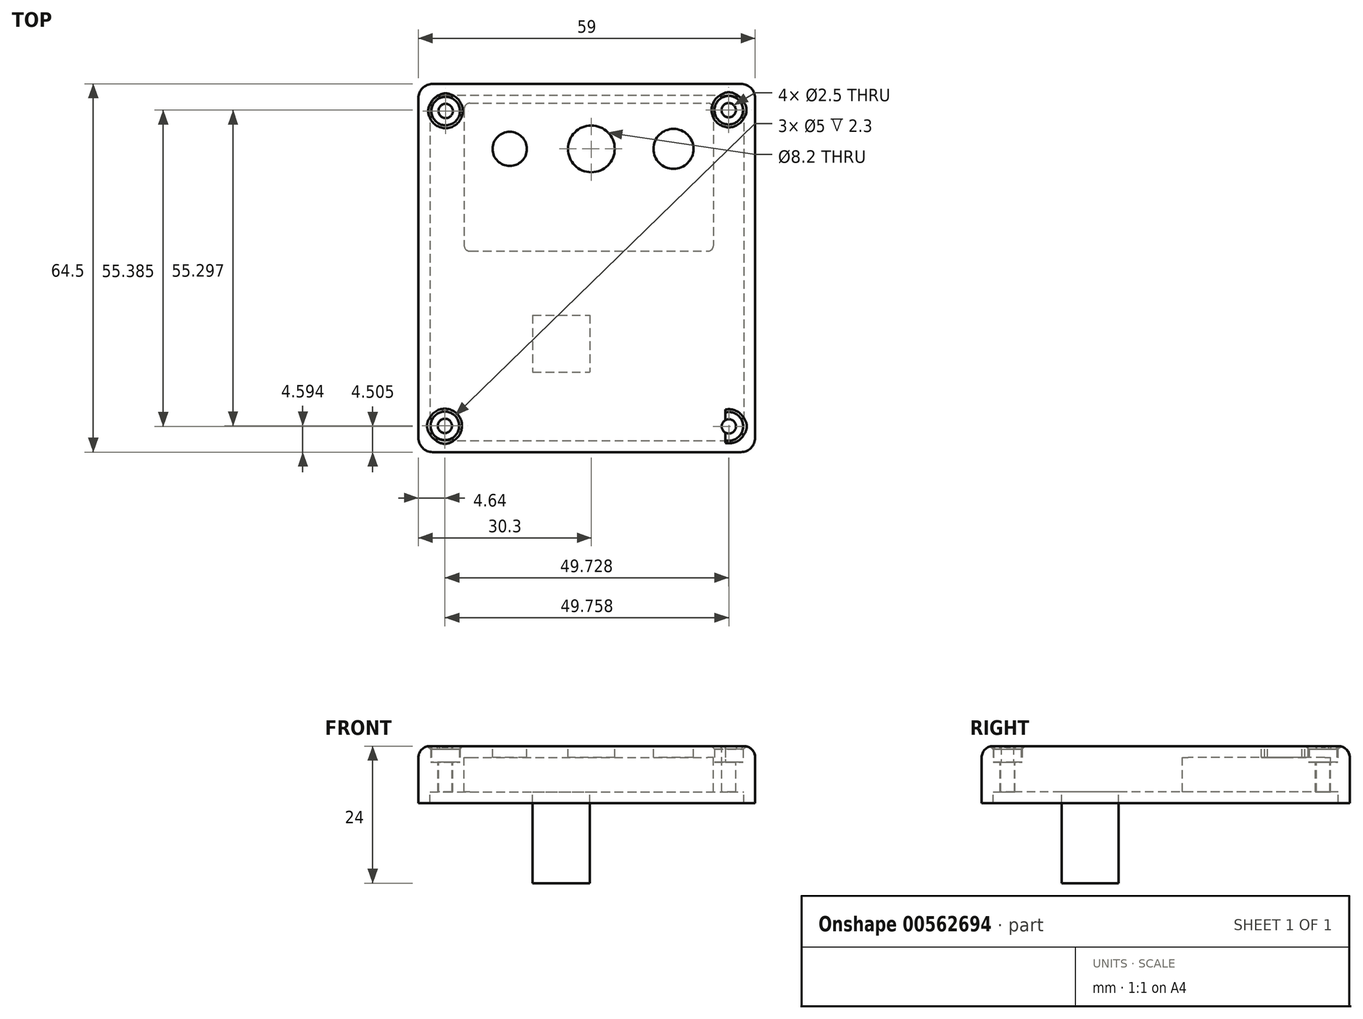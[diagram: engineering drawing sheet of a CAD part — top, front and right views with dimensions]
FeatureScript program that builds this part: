
annotation { "Feature Type Name" : "Feature", "Feature Type Description" : "" }
export const myFeature = defineFeature(function(context is Context, id is Id, definition is map)
    precondition{}
    {
        {
            var Q0;
            Q0=qCreatedBy(makeId("Top.planeOp"),FACE);
            var sketch = newSketch(context, id + "F0", { "sketchPlane" : qUnion([Q0])});
            skLineSegment(sketch, "E0.bottom", {"start": v(-36.58, 47.75) * mm, "end": v(22.42, 47.75) * mm});
            skLineSegment(sketch, "E0.top", {"start": v(-36.58, -16.75) * mm, "end": v(22.42, -16.75) * mm});
            skLineSegment(sketch, "E0.left", {"start": v(-36.58, 47.75) * mm, "end": v(-36.58, -16.75) * mm});
            skLineSegment(sketch, "E0.right", {"start": v(22.42, 47.75) * mm, "end": v(22.42, -16.75) * mm});
            skLineSegment(sketch, "E1.bottom", {"start": v(-34.58, 45.75) * mm, "end": v(20.42, 45.75) * mm});
            skLineSegment(sketch, "E1.top", {"start": v(-34.58, -14.75) * mm, "end": v(20.42, -14.75) * mm});
            skLineSegment(sketch, "E1.left", {"start": v(-34.58, 45.75) * mm, "end": v(-34.58, -14.75) * mm});
            skLineSegment(sketch, "E1.right", {"start": v(20.42, 45.75) * mm, "end": v(20.42, -14.75) * mm});
            skLineSegment(sketch, "E2.right", {"start": v(-34.58, -2) * mm, "end": v(-34.58, 2) * mm});
            skLineSegment(sketch, "E3.bottom", {"start": v(-34.58, 45.75) * mm, "end": v(9.72, 45.75) * mm});
            skLineSegment(sketch, "E4.top", {"start": v(-34.58, -14.75) * mm, "end": v(-32.58, -14.75) * mm});
            skLineSegment(sketch, "E4.left", {"start": v(-34.58, -8.75) * mm, "end": v(-34.58, -14.75) * mm});
            skLineSegment(sketch, "E5.bottom", {"start": v(13.36, 45.75) * mm, "end": v(14.86, 45.75) * mm});
            skLineSegment(sketch, "E6.top", {"start": v(16.3, -14.75) * mm, "end": v(14.92, -14.75) * mm});
            skLineSegment(sketch, "E7.bottom", {"start": v(17.21, 9.77) * mm, "end": v(11.21, 9.77) * mm});
            skLineSegment(sketch, "E7.top", {"start": v(17.21, 4.77) * mm, "end": v(11.21, 4.77) * mm});
            skLineSegment(sketch, "E7.left", {"start": v(17.21, 9.77) * mm, "end": v(17.21, 4.77) * mm});
            skLineSegment(sketch, "E7.right", {"start": v(11.21, 9.77) * mm, "end": v(11.21, 4.77) * mm});
            skCircle(sketch, "E8", {"center": v(-31.94, -12.16) * mm, "radius": 1.25 * mm});
            skCircle(sketch, "E9", {"center": v(-31.8, 43) * mm, "radius": 2.5 * mm});
            skCircle(sketch, "E10", {"center": v(-31.8, 43) * mm, "radius": 1.25 * mm});
            skLineSegment(sketch, "E11", {"start": v(-29.3, 43) * mm, "end": v(-29.3, 45.75) * mm});
            skLineSegment(sketch, "E12.bottom", {"start": v(17.22, 16.75) * mm, "end": v(-34.58, 16.75) * mm});
            skLineSegment(sketch, "E12.top", {"start": v(17.22, 15.25) * mm, "end": v(-34.58, 15.25) * mm});
            skLineSegment(sketch, "E12.left", {"start": v(17.22, 15.25) * mm, "end": v(17.22, 16.75) * mm});
            skLineSegment(sketch, "E12.right", {"start": v(-34.58, 15.25) * mm, "end": v(-34.58, 16.75) * mm});
            skLineSegment(sketch, "E13.bottom", {"start": v(-34.58, 14.63) * mm, "end": v(-32.58, 14.63) * mm});
            skLineSegment(sketch, "E13.top", {"start": v(-34.58, 8.63) * mm, "end": v(-32.58, 8.63) * mm});
            skLineSegment(sketch, "E13.left", {"start": v(-34.58, 14.63) * mm, "end": v(-34.58, 8.63) * mm});
            skLineSegment(sketch, "E13.right", {"start": v(-32.58, 14.63) * mm, "end": v(-32.58, 8.63) * mm});
            skCircle(sketch, "E14", {"center": v(17.79, 43.14) * mm, "radius": 2.5 * mm});
            skCircle(sketch, "E15", {"center": v(17.79, 43.14) * mm, "radius": 1.25 * mm});
            skLineSegment(sketch, "E16", {"start": v(17.79, 40.64) * mm, "end": v(20.42, 40.64) * mm});
            skCircle(sketch, "E17", {"center": v(17.82, -12.24) * mm, "radius": 2.5 * mm});
            skCircle(sketch, "E18", {"center": v(17.82, -12.24) * mm, "radius": 1.25 * mm});
            skLineSegment(sketch, "E19", {"start": v(17.82, -9.74) * mm, "end": v(20.42, -9.74) * mm});
            skLineSegment(sketch, "E20.bottom", {"start": v(14.92, -14.75) * mm, "end": v(13.15, -14.75) * mm});
            skLineSegment(sketch, "E20.top", {"start": v(14.92, -13.29) * mm, "end": v(13.15, -13.29) * mm});
            skLineSegment(sketch, "E20.left", {"start": v(14.92, -14.75) * mm, "end": v(14.92, -13.29) * mm});
            skLineSegment(sketch, "E20.right", {"start": v(13.15, -14.75) * mm, "end": v(13.15, -13.29) * mm});
            skLineSegment(sketch, "E21", {"start": v(17.22, 45.75) * mm, "end": v(17.22, -14.75) * mm});
            skLineSegment(sketch, "E22", {"start": v(20.42, -9.02) * mm, "end": v(17.22, -9.02) * mm});
            skLineSegment(sketch, "E23.top", {"start": v(14.92, -7.79) * mm, "end": v(13.15, -7.79) * mm});
            skLineSegment(sketch, "E23.left", {"start": v(14.92, -13.29) * mm, "end": v(14.92, -7.79) * mm});
            skLineSegment(sketch, "E23.right", {"start": v(13.15, -13.29) * mm, "end": v(13.15, -7.79) * mm});
            skLineSegment(sketch, "E24", {"start": v(15.29, 43.14) * mm, "end": v(15.29, 45.75) * mm});
            skLineSegment(sketch, "E25", {"start": v(15.32, -12.24) * mm, "end": v(15.32, -14.75) * mm});
            skLineSegment(sketch, "E26.bottom", {"start": v(-19.58, -1.75) * mm, "end": v(5.42, -1.75) * mm});
            skLineSegment(sketch, "E26.top", {"start": v(-19.58, 7.25) * mm, "end": v(5.42, 7.25) * mm});
            skLineSegment(sketch, "E26.left", {"start": v(-19.58, -1.75) * mm, "end": v(-19.58, 7.25) * mm});
            skLineSegment(sketch, "E26.right", {"start": v(5.42, -1.75) * mm, "end": v(5.42, 7.25) * mm});
            skCircle(sketch, "E27", {"center": v(8.11, 36.36) * mm, "radius": 3.5 * mm});
            skLineSegment(sketch, "E28", {"start": v(-29.58, 15.25) * mm, "end": v(-29.58, -14.75) * mm, "construction": true});
            skLineSegment(sketch, "E29", {"start": v(17.22, 1.25) * mm, "end": v(-34.58, 1.25) * mm, "construction": true});
            skLineSegment(sketch, "E30", {"start": v(-34.58, 6.25) * mm, "end": v(17.21, 6.25) * mm, "construction": true});
            skLineSegment(sketch, "E31.right", {"start": v(8.3, -10.55) * mm, "end": v(8.3, -13.55) * mm});
            skCircle(sketch, "E32", {"center": v(-31.94, -12.16) * mm, "radius": 2.5 * mm});
            skLineSegment(sketch, "E33.bottom", {"start": v(-28.56, 44.36) * mm, "end": v(15.11, 44.36) * mm});
            skLineSegment(sketch, "E33.top", {"start": v(-28.56, 18.44) * mm, "end": v(15.11, 18.44) * mm});
            skLineSegment(sketch, "E33.left", {"start": v(-28.56, 44.36) * mm, "end": v(-28.56, 18.44) * mm});
            skLineSegment(sketch, "E33.right", {"start": v(15.11, 44.36) * mm, "end": v(15.11, 18.44) * mm});
            skLineSegment(sketch, "E34", {"start": v(-31.8, 40.5) * mm, "end": v(-34.58, 40.5) * mm});
            skLineSegment(sketch, "E35.bottom", {"start": v(-20, -2.24) * mm, "end": v(5.9, -2.24) * mm});
            skLineSegment(sketch, "E35.top", {"start": v(-20, 7.67) * mm, "end": v(5.9, 7.67) * mm});
            skLineSegment(sketch, "E35.left", {"start": v(-20, -2.24) * mm, "end": v(-20, 7.67) * mm});
            skLineSegment(sketch, "E35.right", {"start": v(5.9, -2.24) * mm, "end": v(5.9, 7.67) * mm});
            skCircle(sketch, "E36", {"center": v(-20.58, 36.36) * mm, "radius": 3 * mm});
            skPoint(sketch, "E37.oppositeSnap0", {"position": v(13.15, -10.54) * mm});
            skLineSegment(sketch, "E37.bottom", {"start": v(8.3, -13.55) * mm, "end": v(12.3, -13.55) * mm});
            skLineSegment(sketch, "E37.top", {"start": v(8.3, -10.54) * mm, "end": v(12.3, -10.54) * mm});
            skLineSegment(sketch, "E37.left", {"start": v(8.3, -13.55) * mm, "end": v(8.3, -10.54) * mm});
            skLineSegment(sketch, "E37.right", {"start": v(12.3, -13.55) * mm, "end": v(12.3, -10.54) * mm});
            skLineSegment(sketch, "E38", {"start": v(12.3, -13.55) * mm, "end": v(12.3, 17.84) * mm, "construction": true});
            skLineSegment(sketch, "E39.bottom", {"start": v(12.3, 15.25) * mm, "end": v(8.3, 15.25) * mm});
            skLineSegment(sketch, "E39.top", {"start": v(12.3, 13.25) * mm, "end": v(8.3, 13.25) * mm});
            skLineSegment(sketch, "E39.left", {"start": v(12.3, 15.25) * mm, "end": v(12.3, 13.25) * mm});
            skLineSegment(sketch, "E39.right", {"start": v(8.3, 15.25) * mm, "end": v(8.3, 13.25) * mm});
            skLineSegment(sketch, "E40", {"start": v(-6.28, 41.9) * mm, "end": v(-6.28, 32.7) * mm, "construction": true});
            skLineSegment(sketch, "E41", {"start": v(8.11, 36.36) * mm, "end": v(-21.69, 36.36) * mm, "construction": true});
            skCircle(sketch, "E42", {"center": v(-6.28, 36.36) * mm, "radius": 4.1 * mm});
            skSolve(sketch);
        }
        {
            var Q0;
            Q0=qCreatedBy(makeId("Top.planeOp"),FACE);
            var sketch = newSketch(context, id + "F1", { "sketchPlane" : qUnion([Q0])});
            skLineSegment(sketch, "E43.bottom", {"start": v(-36.58, 47.75) * mm, "end": v(22.42, 47.75) * mm});
            skLineSegment(sketch, "E43.top", {"start": v(-36.58, -16.75) * mm, "end": v(22.42, -16.75) * mm});
            skLineSegment(sketch, "E43.left", {"start": v(-36.58, 47.75) * mm, "end": v(-36.58, -16.75) * mm});
            skLineSegment(sketch, "E43.right", {"start": v(22.42, 47.75) * mm, "end": v(22.42, -16.75) * mm});
            skLineSegment(sketch, "E44.bottom", {"start": v(-34.58, 45.75) * mm, "end": v(20.42, 45.75) * mm});
            skLineSegment(sketch, "E44.top", {"start": v(-34.58, -14.75) * mm, "end": v(20.42, -14.75) * mm});
            skLineSegment(sketch, "E44.left", {"start": v(-34.58, 45.75) * mm, "end": v(-34.58, -14.75) * mm});
            skLineSegment(sketch, "E44.right", {"start": v(20.42, 45.75) * mm, "end": v(20.42, -14.75) * mm});
            skSolve(sketch);
        }
        {
            var Q0;
            Q0=qCreatedBy(makeId("Top.planeOp"),FACE);
            var sketch = newSketch(context, id + "F2", { "sketchPlane" : qUnion([Q0])});
            skLineSegment(sketch, "E45.bottom", {"start": v(-32.68, -7.56) * mm, "end": v(-26.46, -7.56) * mm});
            skLineSegment(sketch, "E45.top", {"start": v(-32.68, 10.68) * mm, "end": v(-26.46, 10.68) * mm});
            skLineSegment(sketch, "E45.left", {"start": v(-32.68, -7.56) * mm, "end": v(-32.68, 10.68) * mm});
            skLineSegment(sketch, "E45.right", {"start": v(-26.46, -7.56) * mm, "end": v(-26.46, 10.68) * mm});
            skSolve(sketch);
        }
        {
            var Q0;
            Q0=qCreatedBy(makeId("Top.planeOp"),FACE);
            var sketch = newSketch(context, id + "F3", { "sketchPlane" : qUnion([Q0])});
            skLineSegment(sketch, "E46.bottom", {"start": v(-36.58, 47.75) * mm, "end": v(22.42, 47.75) * mm});
            skLineSegment(sketch, "E46.top", {"start": v(-36.58, -16.75) * mm, "end": v(22.42, -16.75) * mm});
            skLineSegment(sketch, "E46.left", {"start": v(-36.58, 47.75) * mm, "end": v(-36.58, -16.75) * mm});
            skLineSegment(sketch, "E46.right", {"start": v(22.42, 47.75) * mm, "end": v(22.42, -16.75) * mm});
            skLineSegment(sketch, "E47", {"start": v(-29.58, 14.75) * mm, "end": v(-29.58, -29.34) * mm, "construction": true});
            skLineSegment(sketch, "E48", {"start": v(20.42, -4.25) * mm, "end": v(-34.58, -4.25) * mm, "construction": true});
            skLineSegment(sketch, "E49", {"start": v(17.22, 1.75) * mm, "end": v(-34.58, 1.75) * mm, "construction": true});
            skLineSegment(sketch, "E50", {"start": v(-34.58, 7.75) * mm, "end": v(-24.59, 7.75) * mm, "construction": true});
            skCircle(sketch, "E51", {"center": v(-29.58, -4.25) * mm, "radius": 2 * mm});
            skCircle(sketch, "E52", {"center": v(-29.58, 1.75) * mm, "radius": 2 * mm});
            skCircle(sketch, "E53", {"center": v(-29.58, 7.75) * mm, "radius": 2 * mm});
            skCircle(sketch, "E54", {"center": v(-29.58, 7.75) * mm, "radius": 2.75 * mm});
            skCircle(sketch, "E55", {"center": v(-29.58, 1.75) * mm, "radius": 2.75 * mm});
            skCircle(sketch, "E56", {"center": v(-29.58, -4.25) * mm, "radius": 2.75 * mm});
            skSolve(sketch);
        }
        {
            var Q0;
            Q0=makeQuery(id+"F1.imprint","IMPRINT",FACE,{"disambiguationData":[TD([[makeQuery(id+"F1.imprint","IMPRINT",EDGE,{"derivedFrom":sQuery(id+"F1.wireOp",EDGE,"E44.bottom")}),-1.0]])]});
            extrude(context, id + "F4", {"entities" : qUnion([Q0]), "oppositeDirection" : true, "depth" : 8 * mm});
        }
        {
            var Q0;
            Q0=makeQuery(id+"F1.imprint","IMPRINT",FACE,{"disambiguationData":[TD([[makeQuery(id+"F1.imprint","IMPRINT",EDGE,{"derivedFrom":sQuery(id+"F1.wireOp",EDGE,"E43.bottom")}),-1.0]])]});
            extrude(context, id + "F5", {"entities" : qUnion([Q0]), "operationType" : NewBodyOperationType.ADD, "oppositeDirection" : true, "depth" : 10 * mm});
        }
        {
            var Q0;
            {var subQ0=sQuery(id+"F0.wireOp",EDGE,"E8");var subQ1=sQuery(id+"F0.wireOp",EDGE,"E4.right");var subQ2=makeQuery(id+"F0.imprint","INTERSECT",VERTEX,{"disambiguationData":[OD(0.0)],"derivedFrom":[subQ1,subQ0]});Q0=makeQuery(id+"F0.imprint","IMPRINT",FACE,{"disambiguationData":[TD([[makeQuery(id+"F0.imprint","IMPRINT",EDGE,{"disambiguationData":[TD([[subQ2,-1.0]])],"derivedFrom":subQ1}),1.0]])]});}
            var Q1;
            {var subQ0=sQuery(id+"F0.wireOp",EDGE,"E8");var subQ1=sQuery(id+"F0.wireOp",EDGE,"E4.right");var subQ2=makeQuery(id+"F0.imprint","INTERSECT",VERTEX,{"disambiguationData":[OD(0.0)],"derivedFrom":[subQ1,subQ0]});Q1=makeQuery(id+"F0.imprint","IMPRINT",FACE,{"disambiguationData":[TD([[makeQuery(id+"F0.imprint","IMPRINT",EDGE,{"disambiguationData":[TD([[subQ2,-1.0]])],"derivedFrom":subQ1}),-1.0]])]});}
            var Q2;
            Q2=makeQuery(id+"F0.imprint","IMPRINT",FACE,{"disambiguationData":[TD([[makeQuery(id+"F0.imprint","IMPRINT",EDGE,{"derivedFrom":sQuery(id+"F0.wireOp",EDGE,"E10")}),1.0]])]});
            var Q3;
            {var subQ0=sQuery(id+"F0.wireOp",EDGE,"E21");var subQ1=sQuery(id+"F0.wireOp",EDGE,"E18");var subQ2=makeQuery(id+"F0.imprint","INTERSECT",VERTEX,{"disambiguationData":[OD(0.0)],"derivedFrom":[subQ1,subQ0]});Q3=makeQuery(id+"F0.imprint","IMPRINT",FACE,{"disambiguationData":[TD([[makeQuery(id+"F0.imprint","IMPRINT",EDGE,{"disambiguationData":[TD([[subQ2,1.0]])],"derivedFrom":subQ1}),1.0]])]});}
            var Q4;
            {var subQ0=sQuery(id+"F0.wireOp",EDGE,"E21");var subQ1=sQuery(id+"F0.wireOp",EDGE,"E18");var subQ2=makeQuery(id+"F0.imprint","INTERSECT",VERTEX,{"disambiguationData":[OD(0.0)],"derivedFrom":[subQ1,subQ0]});Q4=makeQuery(id+"F0.imprint","IMPRINT",FACE,{"disambiguationData":[TD([[makeQuery(id+"F0.imprint","IMPRINT",EDGE,{"disambiguationData":[TD([[subQ2,-1.0]])],"derivedFrom":subQ1}),1.0]])]});}
            var Q5;
            Q5=makeQuery(id+"F0.imprint","IMPRINT",FACE,{"disambiguationData":[TD([[makeQuery(id+"F0.imprint","IMPRINT",EDGE,{"derivedFrom":sQuery(id+"F0.wireOp",EDGE,"E27")}),1.0]])]});
            var Q6;
            {var subQ0=sQuery(id+"F0.wireOp",EDGE,"E21");var subQ1=sQuery(id+"F0.wireOp",EDGE,"E15");var subQ2=makeQuery(id+"F0.imprint","INTERSECT",VERTEX,{"disambiguationData":[OD(0.0)],"derivedFrom":[subQ1,subQ0]});Q6=makeQuery(id+"F0.imprint","IMPRINT",FACE,{"disambiguationData":[TD([[makeQuery(id+"F0.imprint","IMPRINT",EDGE,{"disambiguationData":[TD([[subQ2,1.0]])],"derivedFrom":subQ1}),1.0]])]});}
            var Q7;
            {var subQ0=sQuery(id+"F0.wireOp",EDGE,"E21");var subQ1=sQuery(id+"F0.wireOp",EDGE,"E15");var subQ2=makeQuery(id+"F0.imprint","INTERSECT",VERTEX,{"disambiguationData":[OD(0.0)],"derivedFrom":[subQ1,subQ0]});Q7=makeQuery(id+"F0.imprint","IMPRINT",FACE,{"disambiguationData":[TD([[makeQuery(id+"F0.imprint","IMPRINT",EDGE,{"disambiguationData":[TD([[subQ2,-1.0]])],"derivedFrom":subQ1}),1.0]])]});}
            var Q8;
            Q8=makeQuery(id+"F0.imprint","IMPRINT",FACE,{"disambiguationData":[TD([[makeQuery(id+"F0.imprint","IMPRINT",EDGE,{"derivedFrom":sQuery(id+"F0.wireOp",EDGE,"E8")}),1.0]])]});
            extrude(context, id + "F6", {"entities" : qUnion([Q0, Q1, Q2, Q3, Q4, Q5, Q6, Q7, Q8]), "operationType" : NewBodyOperationType.REMOVE, "oppositeDirection" : true, "depth" : 9.6 * mm});
        }
        {
            var Q0;
            Q0=makeQuery(id+"F2.imprint","IMPRINT",FACE,{"disambiguationData":[TD([[makeQuery(id+"F2.imprint","IMPRINT",EDGE,{"derivedFrom":sQuery(id+"F2.wireOp",EDGE,"E45.bottom")}),1.0]])]});
            extrude(context, id + "F7", {"entities" : qUnion([Q0]), "operationType" : NewBodyOperationType.ADD, "oppositeDirection" : true, "depth" : 4.07 * mm});
        }
        {
            var Q0;
            Q0=makeQuery(id+"F5.opExtrude","SWEPT_EDGE",EDGE,{"disambiguationData":[OSD([sQuery(id+"F1.wireOp",EDGE,"E43.top"),sQuery(id+"F1.wireOp",EDGE,"E43.right")])]});
            var Q1;
            Q1=makeQuery(id+"F5.opExtrude","SWEPT_EDGE",EDGE,{"disambiguationData":[OSD([sQuery(id+"F1.wireOp",EDGE,"E43.bottom"),sQuery(id+"F1.wireOp",EDGE,"E43.right")])]});
            var Q2;
            Q2=makeQuery(id+"F5.opExtrude","SWEPT_EDGE",EDGE,{"disambiguationData":[OSD([sQuery(id+"F1.wireOp",EDGE,"E43.top"),sQuery(id+"F1.wireOp",EDGE,"E43.left")])]});
            var Q3;
            Q3=makeQuery(id+"F5.opExtrude","SWEPT_EDGE",EDGE,{"disambiguationData":[OSD([sQuery(id+"F1.wireOp",EDGE,"E43.bottom"),sQuery(id+"F1.wireOp",EDGE,"E43.left")])]});
            fillet(context, id + "F8", {"entities" : qUnion([Q0, Q1, Q2, Q3]), "radius" : 2.5 * mm, "tangentPropagation" : true, "allowEdgeOverflow" : false});
        }
        {
            var Q0;
            Q0=makeQuery(id+"F0.imprint","IMPRINT",FACE,{"disambiguationData":[TD([[makeQuery(id+"F0.imprint","IMPRINT",EDGE,{"derivedFrom":sQuery(id+"F0.wireOp",EDGE,"E27")}),-1.0]])]});
            extrude(context, id + "F9", {"entities" : qUnion([Q0]), "operationType" : NewBodyOperationType.REMOVE, "oppositeDirection" : true, "depth" : 25 * mm, "hasSecondDirection" : true, "secondDirectionOppositeDirection" : true, "secondDirectionDepth" : 2 * mm});
        }
        {
            var Q0;
            {var subQ4=sQuery(id+"F0.wireOp",EDGE,"E17");var subQ5=makeQuery(id+"F0.imprint","INTERSECT",VERTEX,{"derivedFrom":[subQ4,sQuery(id+"F0.wireOp",EDGE,"E25")]});Q0=makeQuery(id+"F0.imprint","IMPRINT",FACE,{"disambiguationData":[TD([[makeQuery(id+"F0.imprint","IMPRINT",EDGE,{"disambiguationData":[TD([[subQ5,1.0]])],"derivedFrom":subQ4}),1.0]])]});}
            var Q1;
            {var subQ1=sQuery(id+"F0.wireOp",EDGE,"E17");var subQ6=makeQuery(id+"F0.imprint","INTERSECT",VERTEX,{"derivedFrom":[subQ1,sQuery(id+"F0.wireOp",EDGE,"E19")]});Q1=makeQuery(id+"F0.imprint","IMPRINT",FACE,{"disambiguationData":[TD([[makeQuery(id+"F0.imprint","IMPRINT",EDGE,{"disambiguationData":[TD([[subQ6,-1.0]])],"derivedFrom":subQ1}),1.0]])]});}
            var Q2;
            Q2=makeQuery(id+"F0.imprint","IMPRINT",FACE,{"disambiguationData":[TD([[makeQuery(id+"F0.imprint","IMPRINT",EDGE,{"derivedFrom":sQuery(id+"F0.wireOp",EDGE,"E10")}),-1.0]])]});
            var Q3;
            {var subQ0=sQuery(id+"F0.wireOp",EDGE,"PLKqhVFR-8eKu-Ixv1-GPgQ-gXaM0qRD25Is");var subQ2=sQuery(id+"F0.wireOp",EDGE,"E4.right");var subQ7=makeQuery(id+"F0.imprint","INTERSECT",VERTEX,{"disambiguationData":[OD(0.0)],"derivedFrom":[subQ2,subQ0]});Q3=makeQuery(id+"F0.imprint","IMPRINT",FACE,{"disambiguationData":[TD([[makeQuery(id+"F0.imprint","IMPRINT",EDGE,{"disambiguationData":[TD([[subQ7,-1.0]])],"derivedFrom":subQ2}),1.0]])]});}
            var Q4;
            {var subQ0=sQuery(id+"F0.wireOp",EDGE,"PLKqhVFR-8eKu-Ixv1-GPgQ-gXaM0qRD25Is");var subQ1=sQuery(id+"F0.wireOp",EDGE,"E4.right");var subQ2=makeQuery(id+"F0.imprint","INTERSECT",VERTEX,{"disambiguationData":[OD(0.0)],"derivedFrom":[subQ1,subQ0]});Q4=makeQuery(id+"F0.imprint","IMPRINT",FACE,{"disambiguationData":[TD([[makeQuery(id+"F0.imprint","IMPRINT",EDGE,{"disambiguationData":[TD([[subQ2,-1.0]])],"derivedFrom":subQ1}),-1.0]])]});}
            var Q5;
            {var subQ1=sQuery(id+"F0.wireOp",EDGE,"E14");var subQ6=makeQuery(id+"F0.imprint","INTERSECT",VERTEX,{"derivedFrom":[subQ1,sQuery(id+"F0.wireOp",EDGE,"E24")]});Q5=makeQuery(id+"F0.imprint","IMPRINT",FACE,{"disambiguationData":[TD([[makeQuery(id+"F0.imprint","IMPRINT",EDGE,{"disambiguationData":[TD([[subQ6,1.0]])],"derivedFrom":subQ1}),1.0]])]});}
            var Q6;
            {var subQ4=sQuery(id+"F0.wireOp",EDGE,"E14");var subQ6=makeQuery(id+"F0.imprint","INTERSECT",VERTEX,{"derivedFrom":[subQ4,sQuery(id+"F0.wireOp",EDGE,"E16")]});Q6=makeQuery(id+"F0.imprint","IMPRINT",FACE,{"disambiguationData":[TD([[makeQuery(id+"F0.imprint","IMPRINT",EDGE,{"disambiguationData":[TD([[subQ6,1.0]])],"derivedFrom":subQ4}),1.0]])]});}
            var Q7;
            {var subQ3=sQuery(id+"F0.wireOp",EDGE,"E32");var subQ5=sQuery(id+"F0.wireOp",EDGE,"E4.right");var subQ6=makeQuery(id+"F0.imprint","INTERSECT",VERTEX,{"disambiguationData":[OD(0.0)],"derivedFrom":[subQ5,subQ3]});Q7=makeQuery(id+"F0.imprint","IMPRINT",FACE,{"disambiguationData":[TD([[makeQuery(id+"F0.imprint","IMPRINT",EDGE,{"disambiguationData":[TD([[subQ6,-1.0]])],"derivedFrom":subQ5}),1.0]])]});}
            var Q8;
            {var subQ1=sQuery(id+"F0.wireOp",EDGE,"E4.right");var subQ6=sQuery(id+"F0.wireOp",EDGE,"kjhwjDdY-w9so-hjMB-xEs9-QlES4Zc8QczL");var subQ7=makeQuery(id+"F0.imprint","INTERSECT",VERTEX,{"derivedFrom":[subQ1,subQ6]});Q8=makeQuery(id+"F0.imprint","IMPRINT",FACE,{"disambiguationData":[TD([[makeQuery(id+"F0.imprint","IMPRINT",EDGE,{"disambiguationData":[TD([[subQ7,-1.0]])],"derivedFrom":subQ1}),-1.0]])]});}
            var Q9;
            {var subQ0=sQuery(id+"F0.wireOp",EDGE,"E32");var subQ1=sQuery(id+"F0.wireOp",EDGE,"E4.right");var subQ2=makeQuery(id+"F0.imprint","INTERSECT",VERTEX,{"disambiguationData":[OD(0.0)],"derivedFrom":[subQ1,subQ0]});Q9=makeQuery(id+"F0.imprint","IMPRINT",FACE,{"disambiguationData":[TD([[makeQuery(id+"F0.imprint","IMPRINT",EDGE,{"disambiguationData":[TD([[subQ2,-1.0]])],"derivedFrom":subQ1}),-1.0]])]});}
            var Q10;
            Q10=makeQuery(id+"F0.imprint","IMPRINT",FACE,{"disambiguationData":[TD([[makeQuery(id+"F0.imprint","IMPRINT",EDGE,{"derivedFrom":sQuery(id+"F0.wireOp",EDGE,"E8")}),-1.0]])]});
            extrude(context, id + "F10", {"entities" : qUnion([Q0, Q1, Q2, Q3, Q4, Q5, Q6, Q7, Q8, Q9, Q10]), "operationType" : NewBodyOperationType.REMOVE, "depth" : 3.9 * mm, "hasSecondDirection" : true, "secondDirectionOppositeDirection" : true, "secondDirectionDepth" : 2.8 * mm});
        }
        {
            var Q0;
            Q0=makeQuery(id+"F0.imprint","IMPRINT",FACE,{"disambiguationData":[TD([[makeQuery(id+"F0.imprint","IMPRINT",EDGE,{"derivedFrom":sQuery(id+"F0.wireOp",EDGE,"EeBKnc5o-wB0O-0N6T-5B69-5pySvWSWUYzF")}),-1.0]])]});
            var Q1;
            Q1=makeQuery(id+"F0.imprint","IMPRINT",FACE,{"disambiguationData":[TD([[makeQuery(id+"F0.imprint","IMPRINT",EDGE,{"derivedFrom":sQuery(id+"F0.wireOp",EDGE,"E27")}),-1.0]])]});
            extrude(context, id + "F11", {"entities" : qUnion([Q0, Q1]), "operationType" : NewBodyOperationType.REMOVE, "oppositeDirection" : true, "depth" : 15 * mm, "hasSecondDirection" : true, "secondDirectionOppositeDirection" : true, "secondDirectionDepth" : 2 * mm});
        }
        {
            var Q0;
            Q0=makeQuery(id+"F9.boolean.opBoolean","COPY",EDGE,{"derivedFrom":makeQuery(id+"F9.opExtrude","SWEPT_EDGE",EDGE,{"disambiguationData":[OSD([sQuery(id+"F0.wireOp",EDGE,"E33.bottom"),sQuery(id+"F0.wireOp",EDGE,"E33.left")])]})});
            var Q1;
            Q1=makeQuery(id+"F9.boolean.opBoolean","COPY",EDGE,{"derivedFrom":makeQuery(id+"F9.opExtrude","SWEPT_EDGE",EDGE,{"disambiguationData":[OSD([sQuery(id+"F0.wireOp",EDGE,"E33.top"),sQuery(id+"F0.wireOp",EDGE,"E33.left")])]})});
            var Q2;
            Q2=makeQuery(id+"F9.boolean.opBoolean","COPY",EDGE,{"derivedFrom":makeQuery(id+"F9.opExtrude","SWEPT_EDGE",EDGE,{"disambiguationData":[OSD([sQuery(id+"F0.wireOp",EDGE,"E33.top"),sQuery(id+"F0.wireOp",EDGE,"E33.right")])]})});
            var Q3;
            Q3=makeQuery(id+"F9.boolean.opBoolean","COPY",EDGE,{"derivedFrom":makeQuery(id+"F9.opExtrude","SWEPT_EDGE",EDGE,{"disambiguationData":[OSD([sQuery(id+"F0.wireOp",EDGE,"E33.bottom"),sQuery(id+"F0.wireOp",EDGE,"E33.right")])]})});
            fillet(context, id + "F12", {"entities" : qUnion([Q0, Q1, Q2, Q3]), "radius" : 1 * mm, "tangentPropagation" : true, "allowEdgeOverflow" : false});
        }
        {
            var Q0;
            Q0=makeQuery(id+"F5.opExtrude","CAP_EDGE",EDGE,{"disambiguationData":[OSD([sQuery(id+"F1.wireOp",EDGE,"E43.bottom")])],"isStart":true});
            fillet(context, id + "F13", {"entities" : qUnion([Q0]), "radius" : 2 * mm, "tangentPropagation" : true, "allowEdgeOverflow" : false});
        }
        {
            var Q0;
            Q0=makeQuery(id+"F0.imprint","IMPRINT",FACE,{"disambiguationData":[TD([[makeQuery(id+"F0.imprint","IMPRINT",EDGE,{"derivedFrom":sQuery(id+"F0.wireOp",EDGE,"E36")}),1.0]])]});
            var Q1;
            Q1=makeQuery(id+"F0.imprint","IMPRINT",FACE,{"disambiguationData":[TD([[makeQuery(id+"F0.imprint","IMPRINT",EDGE,{"derivedFrom":sQuery(id+"F0.wireOp",EDGE,"E42")}),1.0]])]});
            extrude(context, id + "F14", {"entities" : qUnion([Q0, Q1]), "operationType" : NewBodyOperationType.REMOVE, "oppositeDirection" : true, "depth" : 25 * mm});
        }
        {
            var Q0;
            Q0=qCreatedBy(makeId("Top.planeOp"),FACE);
            var sketch = newSketch(context, id + "F15", { "sketchPlane" : qUnion([Q0])});
            skLineSegment(sketch, "E57.bottom", {"start": v(-16.58, 7.25) * mm, "end": v(-6.58, 7.25) * mm});
            skLineSegment(sketch, "E57.top", {"start": v(-16.58, -2.75) * mm, "end": v(-6.58, -2.75) * mm});
            skLineSegment(sketch, "E57.left", {"start": v(-16.58, 7.25) * mm, "end": v(-16.58, -2.75) * mm});
            skLineSegment(sketch, "E57.right", {"start": v(-6.58, 7.25) * mm, "end": v(-6.58, -2.75) * mm});
            skSolve(sketch);
        }
        {
            var Q0;
            Q0=qSketchRegion(id+"F15",true);
            extrude(context, id + "F16", {"entities" : qUnion([Q0]), "oppositeDirection" : true, "depth" : 24 * mm, "hasSecondDirection" : true, "secondDirectionOppositeDirection" : true, "secondDirectionDepth" : 8 * mm});
        }
        {
            var Q0;
            {var subQ0=sQuery(id+"F1.wireOp",EDGE,"E44.right");var subQ1=sQuery(id+"F1.wireOp",EDGE,"E44.left");var subQ2=sQuery(id+"F1.wireOp",EDGE,"E44.top");var subQ3=sQuery(id+"F1.wireOp",EDGE,"E44.bottom");Q0=makeQuery(id+"F10.boolean.opBoolean","INTERSECT",EDGE,{"derivedFrom":[makeQuery(id+"F5.boolean.opBoolean","MERGE",FACE,{"derivedFrom":[makeQuery(id+"F4.opExtrude","CAP_FACE",FACE,{"disambiguationData":[OSD([subQ3,subQ2,subQ1,subQ0])],"isStart":true}),makeQuery(id+"F5.opExtrude","CAP_FACE",FACE,{"disambiguationData":[OSD([sQuery(id+"F1.wireOp",EDGE,"E43.bottom"),sQuery(id+"F1.wireOp",EDGE,"E43.top"),sQuery(id+"F1.wireOp",EDGE,"E43.left"),sQuery(id+"F1.wireOp",EDGE,"E43.right"),subQ3,subQ2,subQ1,subQ0])],"isStart":true})]}),makeQuery(id+"F10.opExtrude","SWEPT_FACE",FACE,{"disambiguationData":[OSD([sQuery(id+"F0.wireOp",EDGE,"E9")])]})]});}
            var Q1;
            {var subQ0=sQuery(id+"F1.wireOp",EDGE,"E44.right");var subQ1=sQuery(id+"F1.wireOp",EDGE,"E44.left");var subQ2=sQuery(id+"F1.wireOp",EDGE,"E44.top");var subQ3=sQuery(id+"F1.wireOp",EDGE,"E44.bottom");Q1=makeQuery(id+"F10.boolean.opBoolean","INTERSECT",EDGE,{"derivedFrom":[makeQuery(id+"F5.boolean.opBoolean","MERGE",FACE,{"derivedFrom":[makeQuery(id+"F4.opExtrude","CAP_FACE",FACE,{"disambiguationData":[OSD([subQ3,subQ2,subQ1,subQ0])],"isStart":true}),makeQuery(id+"F5.opExtrude","CAP_FACE",FACE,{"disambiguationData":[OSD([sQuery(id+"F1.wireOp",EDGE,"E43.bottom"),sQuery(id+"F1.wireOp",EDGE,"E43.top"),sQuery(id+"F1.wireOp",EDGE,"E43.left"),sQuery(id+"F1.wireOp",EDGE,"E43.right"),subQ3,subQ2,subQ1,subQ0])],"isStart":true})]}),makeQuery(id+"F10.opExtrude","SWEPT_FACE",FACE,{"disambiguationData":[OSD([sQuery(id+"F0.wireOp",EDGE,"E14")])]})]});}
            var Q2;
            {var subQ0=sQuery(id+"F1.wireOp",EDGE,"E44.right");var subQ1=sQuery(id+"F1.wireOp",EDGE,"E44.left");var subQ2=sQuery(id+"F1.wireOp",EDGE,"E44.top");var subQ3=sQuery(id+"F1.wireOp",EDGE,"E44.bottom");Q2=makeQuery(id+"F10.boolean.opBoolean","INTERSECT",EDGE,{"derivedFrom":[makeQuery(id+"F5.boolean.opBoolean","MERGE",FACE,{"derivedFrom":[makeQuery(id+"F4.opExtrude","CAP_FACE",FACE,{"disambiguationData":[OSD([subQ3,subQ2,subQ1,subQ0])],"isStart":true}),makeQuery(id+"F5.opExtrude","CAP_FACE",FACE,{"disambiguationData":[OSD([sQuery(id+"F1.wireOp",EDGE,"E43.bottom"),sQuery(id+"F1.wireOp",EDGE,"E43.top"),sQuery(id+"F1.wireOp",EDGE,"E43.left"),sQuery(id+"F1.wireOp",EDGE,"E43.right"),subQ3,subQ2,subQ1,subQ0])],"isStart":true})]}),makeQuery(id+"F10.opExtrude","SWEPT_FACE",FACE,{"disambiguationData":[OSD([sQuery(id+"F0.wireOp",EDGE,"E17")])]})]});}
            var Q3;
            {var subQ0=sQuery(id+"F1.wireOp",EDGE,"E44.right");var subQ1=sQuery(id+"F1.wireOp",EDGE,"E44.left");var subQ2=sQuery(id+"F1.wireOp",EDGE,"E44.top");var subQ3=sQuery(id+"F1.wireOp",EDGE,"E44.bottom");Q3=makeQuery(id+"F10.boolean.opBoolean","INTERSECT",EDGE,{"derivedFrom":[makeQuery(id+"F5.boolean.opBoolean","MERGE",FACE,{"derivedFrom":[makeQuery(id+"F4.opExtrude","CAP_FACE",FACE,{"disambiguationData":[OSD([subQ3,subQ2,subQ1,subQ0])],"isStart":true}),makeQuery(id+"F5.opExtrude","CAP_FACE",FACE,{"disambiguationData":[OSD([sQuery(id+"F1.wireOp",EDGE,"E43.bottom"),sQuery(id+"F1.wireOp",EDGE,"E43.top"),sQuery(id+"F1.wireOp",EDGE,"E43.left"),sQuery(id+"F1.wireOp",EDGE,"E43.right"),subQ3,subQ2,subQ1,subQ0])],"isStart":true})]}),makeQuery(id+"F10.opExtrude","SWEPT_FACE",FACE,{"disambiguationData":[OSD([sQuery(id+"F0.wireOp",EDGE,"E32")])]})]});}
            chamfer(context, id + "F17", {"entities" : qUnion([Q0, Q1, Q2, Q3]), "width" : .5 * mm, "tangentPropagation" : true});
        }
        {
            var Q0;
            Q0=makeQuery(id+"F5.opExtrude","SWEPT_EDGE",EDGE,{"disambiguationData":[OSD([sQuery(id+"F1.wireOp",EDGE,"E44.bottom"),sQuery(id+"F1.wireOp",EDGE,"E44.right")])]});
            var Q1;
            Q1=makeQuery(id+"F5.opExtrude","SWEPT_EDGE",EDGE,{"disambiguationData":[OSD([sQuery(id+"F1.wireOp",EDGE,"E44.bottom"),sQuery(id+"F1.wireOp",EDGE,"E44.left")])]});
            var Q2;
            Q2=makeQuery(id+"F5.opExtrude","SWEPT_EDGE",EDGE,{"disambiguationData":[OSD([sQuery(id+"F1.wireOp",EDGE,"E44.top"),sQuery(id+"F1.wireOp",EDGE,"E44.left")])]});
            var Q3;
            Q3=makeQuery(id+"F5.opExtrude","SWEPT_EDGE",EDGE,{"disambiguationData":[OSD([sQuery(id+"F1.wireOp",EDGE,"E44.top"),sQuery(id+"F1.wireOp",EDGE,"E44.right")])]});
            fillet(context, id + "F18", {"entities" : qUnion([Q0, Q1, Q2, Q3]), "radius" : 2.5 * mm, "tangentPropagation" : true, "allowEdgeOverflow" : false});
        }
    });
